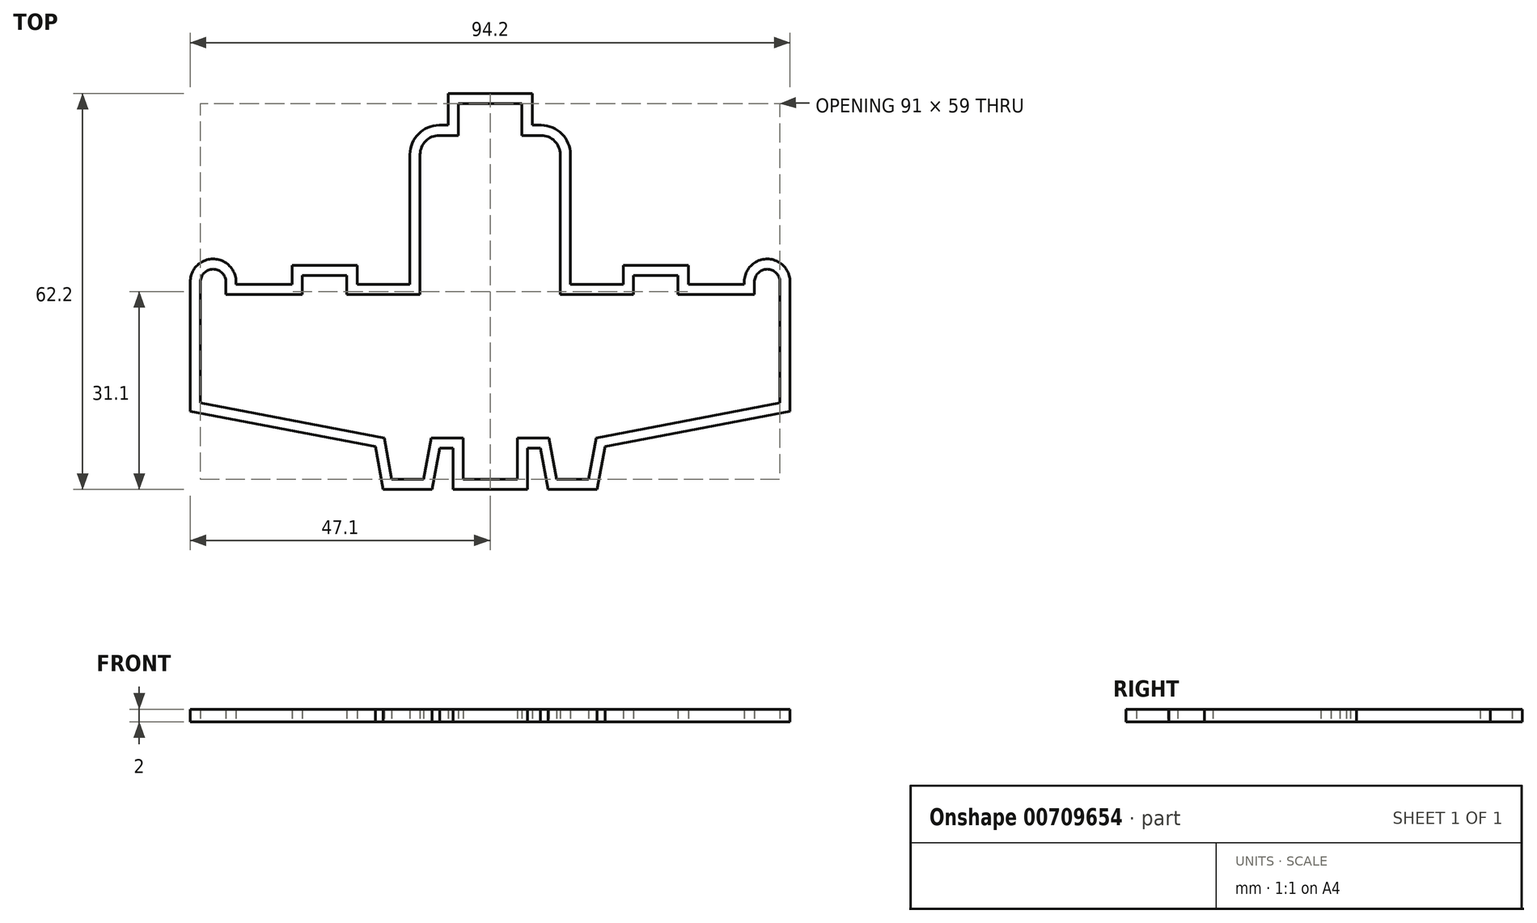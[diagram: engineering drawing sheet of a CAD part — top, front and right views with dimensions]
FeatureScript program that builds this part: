
annotation { "Feature Type Name" : "Feature", "Feature Type Description" : "" }
export const myFeature = defineFeature(function(context is Context, id is Id, definition is map)
    precondition{}
    {
        {
            var Q0;
            Q0=qCreatedBy(makeId("Top.planeOp"),FACE);
            var sketch = newSketch(context, id + "F0", { "sketchPlane" : qUnion([Q0])});
            skLineSegment(sketch, "E0", {"start": v(0, -34.4) * mm, "end": v(0, 45.32) * mm, "construction": true});
            skLineSegment(sketch, "E1", {"start": v(0, 29.5) * mm, "end": v(-5, 29.5) * mm});
            skLineSegment(sketch, "E2", {"start": v(-5, 29.5) * mm, "end": v(-5, 24.5) * mm});
            skLineSegment(sketch, "E3", {"start": v(-5, 24.5) * mm, "end": v(-8, 24.5) * mm});
            skLineSegment(sketch, "E4", {"start": v(-11, 21.5) * mm, "end": v(-11, -0.5) * mm});
            skLineSegment(sketch, "E5", {"start": v(-11, -0.5) * mm, "end": v(-22.5, -0.5) * mm});
            skLineSegment(sketch, "E6", {"start": v(-22.5, -0.5) * mm, "end": v(-22.5, 2.5) * mm});
            skLineSegment(sketch, "E7", {"start": v(-22.5, 2.5) * mm, "end": v(-29.5, 2.5) * mm});
            skLineSegment(sketch, "E8", {"start": v(-29.5, 2.5) * mm, "end": v(-29.5, -0.5) * mm});
            skLineSegment(sketch, "E9", {"start": v(-29.5, -0.5) * mm, "end": v(-41.5, -0.5) * mm});
            skLineSegment(sketch, "E10", {"start": v(-41.5, -0.5) * mm, "end": v(-41.5, 1.5) * mm});
            skLineSegment(sketch, "E11", {"start": v(-43.5, 3.5) * mm, "end": v(-43.5, 3.5) * mm});
            skLineSegment(sketch, "E12", {"start": v(-45.5, 1.5) * mm, "end": v(-45.5, -17.5) * mm});
            skLineSegment(sketch, "E13", {"start": v(0, -29.5) * mm, "end": v(-4.25, -29.5) * mm});
            skLineSegment(sketch, "E14", {"start": v(-4.25, -29.5) * mm, "end": v(-4.25, -23) * mm});
            skLineSegment(sketch, "E15", {"start": v(-4.25, -23) * mm, "end": v(-9.25, -23) * mm});
            skPoint(sketch, "E16.visualSharp", {"position": v(-45.5, 3.5) * mm});
            skArc(sketch, "E16.filletArc", {"start": v(-43.5, 3.5) * mm, "mid": v(-44.91, 2.91) * mm, "end": v(-45.5, 1.5) * mm});
            skPoint(sketch, "E17.visualSharp", {"position": v(-41.5, 3.5) * mm});
            skArc(sketch, "E17.filletArc", {"start": v(-41.5, 1.5) * mm, "mid": v(-42.09, 2.91) * mm, "end": v(-43.5, 3.5) * mm});
            skPoint(sketch, "E18.visualSharp", {"position": v(-11, 24.5) * mm});
            skArc(sketch, "E18.filletArc", {"start": v(-8, 24.5) * mm, "mid": v(-10.12, 23.62) * mm, "end": v(-11, 21.5) * mm});
            skLineSegment(sketch, "E19", {"start": v(-10.45, -29.5) * mm, "end": v(-9.25, -23) * mm});
            skLineSegment(sketch, "E20", {"start": v(-10.45, -29.5) * mm, "end": v(-15.45, -29.5) * mm});
            skLineSegment(sketch, "E21", {"start": v(-15.45, -29.5) * mm, "end": v(-16.65, -23) * mm});
            skLineSegment(sketch, "E22", {"start": v(-45.5, -17.5) * mm, "end": v(-16.65, -23) * mm});
            skLineSegment(sketch, "E23.MirrorCS", {"start": v(22.5, -0.5) * mm, "end": v(22.5, 2.5) * mm});
            skArc(sketch, "E24.MirrorCS", {"start": v(41.5, 1.5) * mm, "mid": v(42.09, 2.91) * mm, "end": v(43.5, 3.5) * mm});
            skLineSegment(sketch, "E25.MirrorCS", {"start": v(5, 24.5) * mm, "end": v(8, 24.5) * mm});
            skLineSegment(sketch, "E26.MirrorCS", {"start": v(29.5, 2.5) * mm, "end": v(29.5, -0.5) * mm});
            skArc(sketch, "E27.MirrorCS", {"start": v(43.5, 3.5) * mm, "mid": v(44.91, 2.91) * mm, "end": v(45.5, 1.5) * mm});
            skLineSegment(sketch, "E28.MirrorCS", {"start": v(41.5, -0.5) * mm, "end": v(41.5, 1.5) * mm});
            skArc(sketch, "E29.MirrorCS", {"start": v(8, 24.5) * mm, "mid": v(10.12, 23.62) * mm, "end": v(11, 21.5) * mm});
            skLineSegment(sketch, "E30.MirrorCS", {"start": v(22.5, 2.5) * mm, "end": v(29.5, 2.5) * mm});
            skLineSegment(sketch, "E31.MirrorCS", {"start": v(4.25, -29.5) * mm, "end": v(4.25, -23) * mm});
            skLineSegment(sketch, "E32.MirrorCS", {"start": v(4.25, -23) * mm, "end": v(9.25, -23) * mm});
            skLineSegment(sketch, "E33.MirrorCS", {"start": v(10.45, -29.5) * mm, "end": v(15.45, -29.5) * mm});
            skLineSegment(sketch, "E34.MirrorCS", {"start": v(5, 29.5) * mm, "end": v(5, 24.5) * mm});
            skLineSegment(sketch, "E35.MirrorCS", {"start": v(29.5, -0.5) * mm, "end": v(41.5, -0.5) * mm});
            skLineSegment(sketch, "E36.MirrorCS", {"start": v(11, -0.5) * mm, "end": v(22.5, -0.5) * mm});
            skLineSegment(sketch, "E37.MirrorCS", {"start": v(0, -29.5) * mm, "end": v(4.25, -29.5) * mm});
            skLineSegment(sketch, "E38.MirrorCS", {"start": v(10.45, -29.5) * mm, "end": v(9.25, -23) * mm});
            skPoint(sketch, "E39.MirrorP", {"position": v(11, 24.5) * mm});
            skPoint(sketch, "E40.MirrorP", {"position": v(41.5, 3.5) * mm});
            skLineSegment(sketch, "E41.MirrorCS", {"start": v(11, 21.5) * mm, "end": v(11, -0.5) * mm});
            skLineSegment(sketch, "E42.MirrorCS", {"start": v(45.5, -17.5) * mm, "end": v(16.65, -23) * mm});
            skPoint(sketch, "E43.MirrorP", {"position": v(45.5, 3.5) * mm});
            skLineSegment(sketch, "E44.MirrorCS", {"start": v(15.45, -29.5) * mm, "end": v(16.65, -23) * mm});
            skLineSegment(sketch, "E45.MirrorCS", {"start": v(0, 29.5) * mm, "end": v(5, 29.5) * mm});
            skLineSegment(sketch, "E46.MirrorCS", {"start": v(45.5, 1.5) * mm, "end": v(45.5, -17.5) * mm});
            skLineSegment(sketch, "E47.0", {"start": v(0, 31.1) * mm, "end": v(-6.6, 31.1) * mm});
            skLineSegment(sketch, "E47.1", {"start": v(0, 31.1) * mm, "end": v(6.6, 31.1) * mm});
            skLineSegment(sketch, "E47.2", {"start": v(6.6, 31.1) * mm, "end": v(6.6, 26.1) * mm});
            skLineSegment(sketch, "E47.3", {"start": v(6.6, 26.1) * mm, "end": v(8, 26.1) * mm});
            skArc(sketch, "E47.4", {"start": v(8, 26.1) * mm, "mid": v(11.25, 24.75) * mm, "end": v(12.6, 21.5) * mm});
            skLineSegment(sketch, "E47.5", {"start": v(12.6, 21.5) * mm, "end": v(12.6, 1.1) * mm});
            skLineSegment(sketch, "E47.6", {"start": v(12.6, 1.1) * mm, "end": v(20.9, 1.1) * mm});
            skLineSegment(sketch, "E47.7", {"start": v(20.9, 1.1) * mm, "end": v(20.9, 4.1) * mm});
            skLineSegment(sketch, "E47.8", {"start": v(20.9, 4.1) * mm, "end": v(31.1, 4.1) * mm});
            skLineSegment(sketch, "E47.9", {"start": v(31.1, 4.1) * mm, "end": v(31.1, 1.1) * mm});
            skLineSegment(sketch, "E47.10", {"start": v(31.1, 1.1) * mm, "end": v(39.92, 1.1) * mm});
            skLineSegment(sketch, "E47.11", {"start": v(-6.6, 31.1) * mm, "end": v(-6.6, 26.1) * mm});
            skArc(sketch, "E47.12", {"start": v(39.92, 1.1) * mm, "mid": v(40.82, 3.9) * mm, "end": v(43.5, 5.1) * mm});
            skArc(sketch, "E47.13", {"start": v(43.5, 5.1) * mm, "mid": v(46.05, 4.05) * mm, "end": v(47.1, 1.5) * mm});
            skLineSegment(sketch, "E47.14", {"start": v(47.1, 1.5) * mm, "end": v(47.1, -18.82) * mm});
            skLineSegment(sketch, "E47.15", {"start": v(47.1, -18.82) * mm, "end": v(18.02, -24.37) * mm});
            skLineSegment(sketch, "E47.16", {"start": v(16.78, -31.1) * mm, "end": v(18.02, -24.37) * mm});
            skLineSegment(sketch, "E47.17", {"start": v(9.12, -31.1) * mm, "end": v(16.78, -31.1) * mm});
            skArc(sketch, "E47.18", {"start": v(-43.5, 5.1) * mm, "mid": v(-46.05, 4.05) * mm, "end": v(-47.1, 1.5) * mm});
            skArc(sketch, "E47.19", {"start": v(-39.92, 1.1) * mm, "mid": v(-40.82, 3.9) * mm, "end": v(-43.5, 5.1) * mm});
            skLineSegment(sketch, "E47.20", {"start": v(-31.1, 1.1) * mm, "end": v(-39.92, 1.1) * mm});
            skLineSegment(sketch, "E47.21", {"start": v(-31.1, 4.1) * mm, "end": v(-31.1, 1.1) * mm});
            skLineSegment(sketch, "E47.22", {"start": v(-20.9, 4.1) * mm, "end": v(-31.1, 4.1) * mm});
            skLineSegment(sketch, "E47.23", {"start": v(-20.9, 1.1) * mm, "end": v(-20.9, 4.1) * mm});
            skLineSegment(sketch, "E47.24", {"start": v(-6.6, 26.1) * mm, "end": v(-8, 26.1) * mm});
            skArc(sketch, "E47.25", {"start": v(-8, 26.1) * mm, "mid": v(-11.25, 24.75) * mm, "end": v(-12.6, 21.5) * mm});
            skLineSegment(sketch, "E47.26", {"start": v(-12.6, 21.5) * mm, "end": v(-12.6, 1.1) * mm});
            skLineSegment(sketch, "E47.27", {"start": v(-12.6, 1.1) * mm, "end": v(-20.9, 1.1) * mm});
            skLineSegment(sketch, "E47.28", {"start": v(-47.1, 1.5) * mm, "end": v(-47.1, -18.82) * mm});
            skLineSegment(sketch, "E47.29", {"start": v(-47.1, -18.82) * mm, "end": v(-18.02, -24.37) * mm});
            skLineSegment(sketch, "E47.30", {"start": v(-16.78, -31.1) * mm, "end": v(-18.02, -24.37) * mm});
            skLineSegment(sketch, "E47.31", {"start": v(-9.12, -31.1) * mm, "end": v(-16.78, -31.1) * mm});
            skLineSegment(sketch, "E47.32", {"start": v(-9.12, -31.1) * mm, "end": v(-7.92, -24.6) * mm});
            skLineSegment(sketch, "E47.33", {"start": v(-5.85, -24.6) * mm, "end": v(-7.92, -24.6) * mm});
            skLineSegment(sketch, "E47.34", {"start": v(-5.85, -31.1) * mm, "end": v(-5.85, -24.6) * mm});
            skLineSegment(sketch, "E47.35", {"start": v(0, -31.1) * mm, "end": v(-5.85, -31.1) * mm});
            skLineSegment(sketch, "E47.36", {"start": v(0, -31.1) * mm, "end": v(5.85, -31.1) * mm});
            skLineSegment(sketch, "E47.37", {"start": v(5.85, -31.1) * mm, "end": v(5.85, -24.6) * mm});
            skLineSegment(sketch, "E47.38", {"start": v(5.85, -24.6) * mm, "end": v(7.92, -24.6) * mm});
            skLineSegment(sketch, "E47.39", {"start": v(9.12, -31.1) * mm, "end": v(7.92, -24.6) * mm});
            skSolve(sketch);
        }
        {
            var Q0;
            Q0=makeQuery(id+"F0.imprint","IMPRINT",FACE,{"disambiguationData":[TD([[makeQuery(id+"F0.imprint","IMPRINT",EDGE,{"derivedFrom":sQuery(id+"F0.wireOp",EDGE,"9IHDfN1N-enht-F21d-N71B-OsCDjcQyuhie.bottom")}),-1.0]])]});
            var Q1;
            Q1=makeQuery(id+"F0.imprint","IMPRINT",FACE,{"disambiguationData":[TD([[makeQuery(id+"F0.imprint","IMPRINT",EDGE,{"derivedFrom":sQuery(id+"F0.wireOp",EDGE,"E1")}),-1.0]])]});
            extrude(context, id + "F1", {"entities" : qUnion([Q0, Q1]), "depth" : 2 * mm, "offsetDistance" : 25 * mm, "symmetric" : true});
        }
    });
